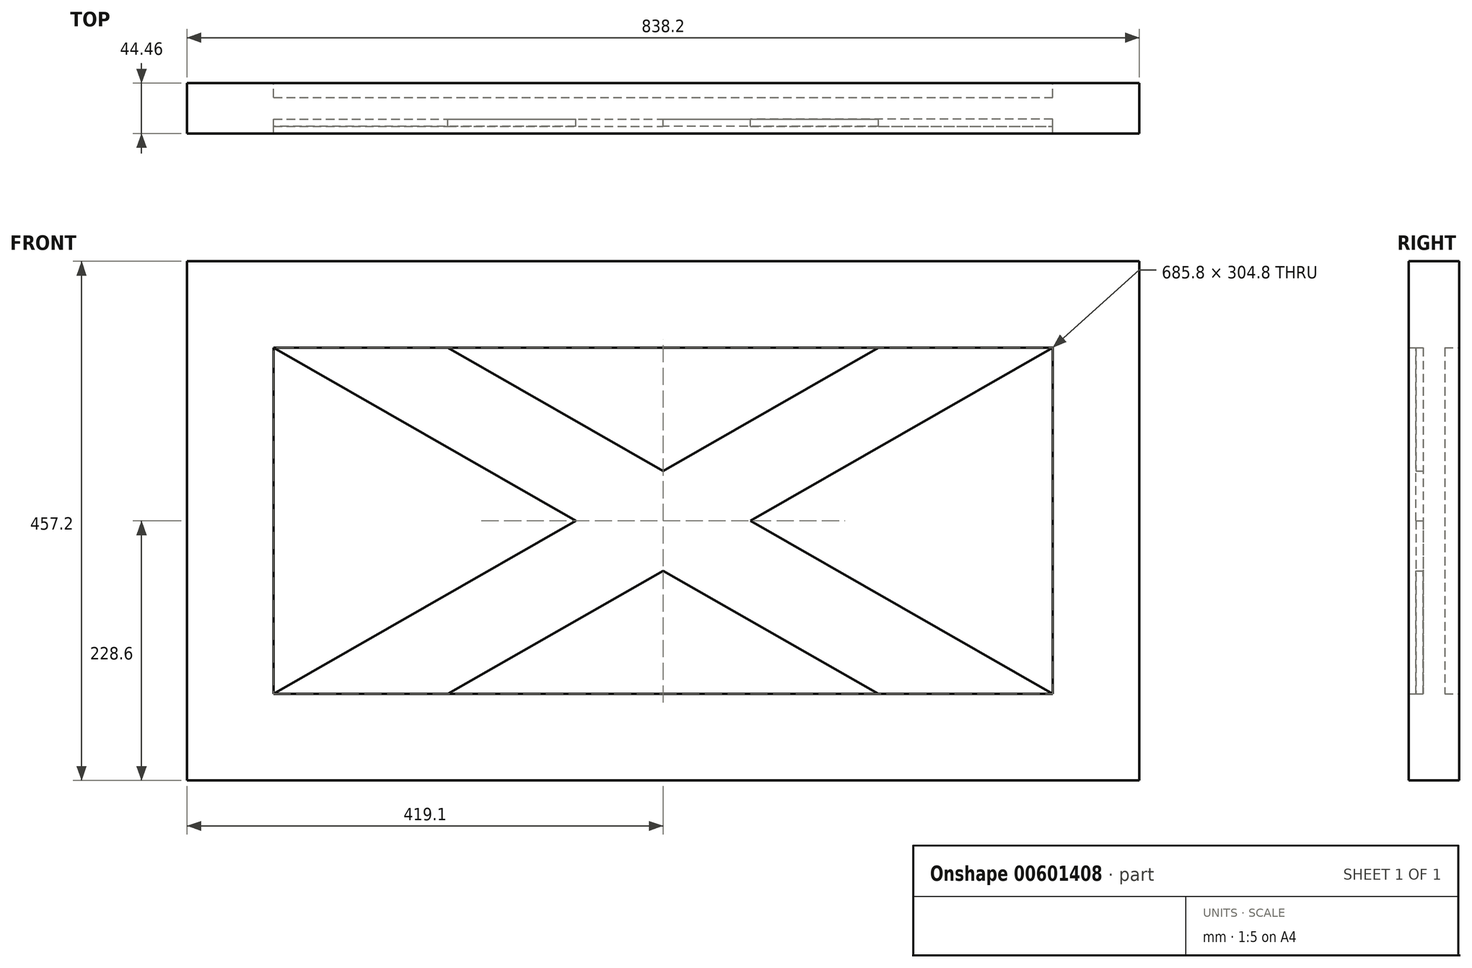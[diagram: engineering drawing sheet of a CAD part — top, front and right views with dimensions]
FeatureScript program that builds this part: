
annotation { "Feature Type Name" : "Feature", "Feature Type Description" : "" }
export const myFeature = defineFeature(function(context is Context, id is Id, definition is map)
    precondition{}
    {
        {
            var Q0;
            Q0=qCreatedBy(makeId("Front.planeOp"),FACE);
            var sketch = newSketch(context, id + "F0", { "sketchPlane" : qUnion([Q0])});
            skLineSegment(sketch, "E0.bottom", {"start": v(-419.1, 228.6) * mm, "end": v(419.1, 228.6) * mm});
            skLineSegment(sketch, "E0.top", {"start": v(-419.1, -228.6) * mm, "end": v(419.1, -228.6) * mm});
            skLineSegment(sketch, "E0.left", {"start": v(-419.1, 228.6) * mm, "end": v(-419.1, -228.6) * mm});
            skLineSegment(sketch, "E0.right", {"start": v(419.1, 228.6) * mm, "end": v(419.1, -228.6) * mm});
            skPoint(sketch, "E0.middle", {"position": v(0, 0) * mm});
            skLineSegment(sketch, "E1.bottom", {"start": v(-342.9, 152.4) * mm, "end": v(342.9, 152.4) * mm});
            skLineSegment(sketch, "E1.top", {"start": v(-342.9, -152.4) * mm, "end": v(342.9, -152.4) * mm});
            skLineSegment(sketch, "E1.left", {"start": v(-342.9, 152.4) * mm, "end": v(-342.9, -152.4) * mm});
            skLineSegment(sketch, "E1.right", {"start": v(342.9, 152.4) * mm, "end": v(342.9, -152.4) * mm});
            skSolve(sketch);
        }
        {
            var Q0;
            Q0=makeQuery(id+"F0.imprint","IMPRINT",FACE,{"disambiguationData":[TD([[makeQuery(id+"F0.imprint","IMPRINT",EDGE,{"derivedFrom":sQuery(id+"F0.wireOp",EDGE,"E0.bottom")}),-1.0]])]});
            extrude(context, id + "F1", {"entities" : qUnion([Q0]), "endBound" : BoundingType.SYMMETRIC, "depth" : 44.45 * mm, "offsetDistance" : 25.4 * mm});
        }
        {
            var Q0;
            Q0=makeQuery(id+"F0.imprint","IMPRINT",FACE,{"disambiguationData":[TD([[makeQuery(id+"F0.imprint","IMPRINT",EDGE,{"derivedFrom":sQuery(id+"F0.wireOp",EDGE,"E1.bottom")}),-1.0]])]});
            extrude(context, id + "F2", {"entities" : qUnion([Q0]), "operationType" : NewBodyOperationType.ADD, "endBound" : BoundingType.SYMMETRIC, "depth" : 19.05 * mm, "offsetDistance" : 25.4 * mm});
        }
        {
            var Q0;
            Q0=makeQuery(id+"F2.opExtrude","CAP_FACE",FACE,{"disambiguationData":[OSD([sQuery(id+"F0.wireOp",EDGE,"E1.bottom"),sQuery(id+"F0.wireOp",EDGE,"E1.top"),sQuery(id+"F0.wireOp",EDGE,"E1.left"),sQuery(id+"F0.wireOp",EDGE,"E1.right")])],"isStart":false});
            var sketch = newSketch(context, id + "F3", { "sketchPlane" : qUnion([Q0])});
            skLineSegment(sketch, "E2", {"start": v(-189.53, 152.4) * mm, "end": v(342.9, -152.4) * mm});
            skLineSegment(sketch, "E3", {"start": v(342.9, -152.4) * mm, "end": v(189.53, -152.4) * mm});
            skLineSegment(sketch, "E4", {"start": v(189.53, -152.4) * mm, "end": v(342.9, -152.4) * mm});
            skLineSegment(sketch, "E5", {"start": v(189.53, -152.4) * mm, "end": v(-342.9, 152.4) * mm});
            skLineSegment(sketch, "E6", {"start": v(-342.9, 152.4) * mm, "end": v(-189.53, 152.4) * mm});
            skSolve(sketch);
        }
        {
            var Q0;
            Q0=makeQuery(id+"F3.imprint","IMPRINT",FACE,{"disambiguationData":[TD([[makeQuery(id+"F3.imprint","IMPRINT",EDGE,{"derivedFrom":sQuery(id+"F3.wireOp",EDGE,"E2")}),-1.0]])]});
            var Q1;
            Q1=sQuery(id+"F3.wireOp",EDGE,"E5");
            var Q2;
            Q2=sQuery(id+"F3.wireOp",EDGE,"E2");
            var Q3;
            Q3=sQuery(id+"F3.wireOp",EDGE,"E6");
            var Q4;
            Q4=sQuery(id+"F3.wireOp",EDGE,"E4");
            var Q5;
            Q5=makeQuery(id+"F1.opExtrude","SWEPT_BODY",BODY,{"disambiguationData":[OSD([sQuery(id+"F0.wireOp",EDGE,"E0.bottom"),sQuery(id+"F0.wireOp",EDGE,"E0.top"),sQuery(id+"F0.wireOp",EDGE,"E0.left"),sQuery(id+"F0.wireOp",EDGE,"E0.right"),sQuery(id+"F0.wireOp",EDGE,"E1.bottom"),sQuery(id+"F0.wireOp",EDGE,"E1.top"),sQuery(id+"F0.wireOp",EDGE,"E1.left"),sQuery(id+"F0.wireOp",EDGE,"E1.right")])]});
            extrude(context, id + "F4", {"entities" : qUnion([Q0]), "operationType" : NewBodyOperationType.ADD, "surfaceEntities" : qUnion([Q1, Q2, Q3, Q4]), "depth" : 6.35 * mm, "endBoundEntityBody" : qUnion([Q5]), "offsetDistance" : 25.4 * mm});
        }
        {
            var Q0;
            {var subQ0=sQuery(id+"F0.wireOp",EDGE,"E1.top");var subQ1=sQuery(id+"F0.wireOp",EDGE,"E1.left");Q0=makeQuery(id+"F4.boolean.opBoolean","SPLIT",FACE,{"disambiguationData":[TD([makeQuery(id+"F1.opExtrude","SWEPT_FACE",FACE,{"disambiguationData":[OSD([subQ0])]})])],"derivedFrom":makeQuery(id+"F2.opExtrude","CAP_FACE",FACE,{"disambiguationData":[OSD([sQuery(id+"F0.wireOp",EDGE,"E1.bottom"),subQ0,subQ1,sQuery(id+"F0.wireOp",EDGE,"E1.right")])],"isStart":false})});}
            var sketch = newSketch(context, id + "F5", { "sketchPlane" : qUnion([Q0])});
            skLineSegment(sketch, "E7", {"start": v(-342.9, -152.4) * mm, "end": v(-76.69, 0) * mm});
            skLineSegment(sketch, "E8", {"start": v(189.53, 152.4) * mm, "end": v(342.9, 152.4) * mm});
            skLineSegment(sketch, "E9", {"start": v(342.9, 152.4) * mm, "end": v(76.69, 0) * mm});
            skLineSegment(sketch, "E10", {"start": v(-189.53, -152.4) * mm, "end": v(-342.9, -152.4) * mm});
            skLineSegment(sketch, "E11", {"start": v(-76.69, 0) * mm, "end": v(0, -43.9) * mm});
            skLineSegment(sketch, "E12", {"start": v(0, 43.9) * mm, "end": v(76.69, 0) * mm});
            skLineSegment(sketch, "E13.trimOffspring", {"start": v(0, 43.9) * mm, "end": v(189.53, 152.4) * mm});
            skLineSegment(sketch, "E14.trimOffspring", {"start": v(0, -43.9) * mm, "end": v(-189.53, -152.4) * mm});
            skSolve(sketch);
        }
        {
            var Q0;
            Q0=makeQuery(id+"F5.imprint","IMPRINT",FACE,{"disambiguationData":[TD([[makeQuery(id+"F5.imprint","IMPRINT",EDGE,{"derivedFrom":sQuery(id+"F5.wireOp",EDGE,"E7")}),-1.0]])]});
            var Q1;
            Q1=makeQuery(id+"F5.imprint","IMPRINT",FACE,{"disambiguationData":[TD([[makeQuery(id+"F5.imprint","IMPRINT",EDGE,{"derivedFrom":sQuery(id+"F5.wireOp",EDGE,"E8")}),-1.0]])]});
            extrude(context, id + "F6", {"entities" : qUnion([Q0, Q1]), "operationType" : NewBodyOperationType.ADD, "depth" : 6.35 * mm, "offsetDistance" : 25.4 * mm});
        }
    });
